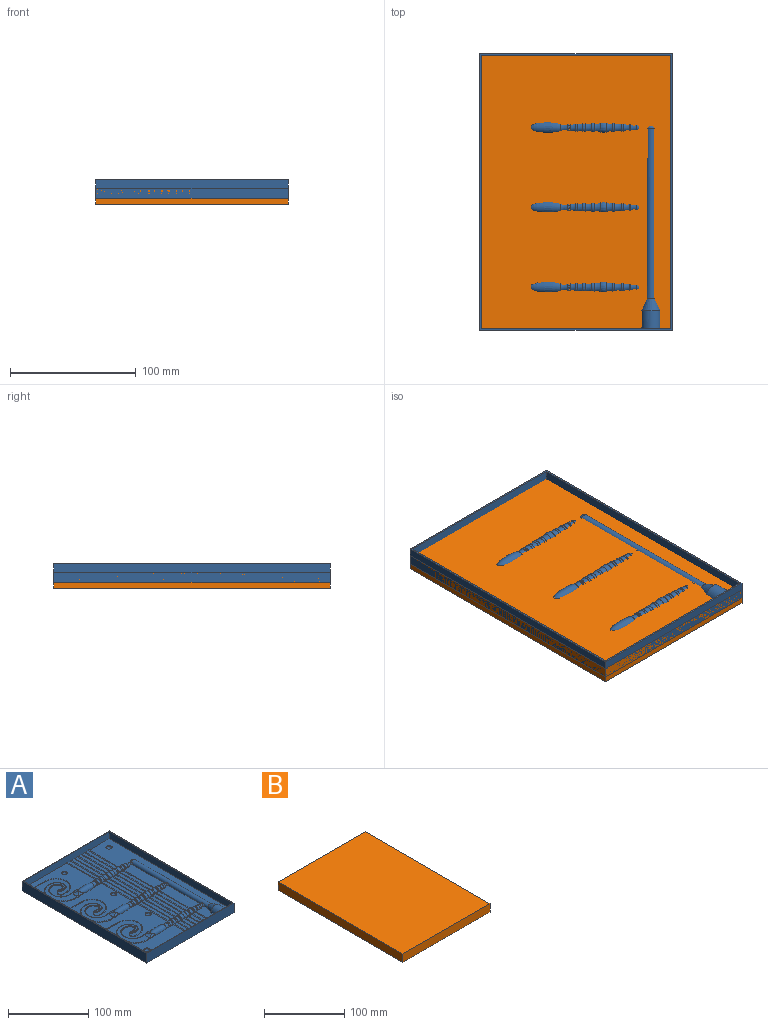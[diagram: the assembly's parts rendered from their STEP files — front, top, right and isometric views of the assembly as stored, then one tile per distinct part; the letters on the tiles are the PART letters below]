
ASSEMBLY  parts=2 mates=1
PART A: 197 faces, bbox 154.9x221.7x16.3 mm
  f0: plane 30.21x16.13mm, normal (0,0,1), area 393mm2, adj f10,f56,f113,f114,f116,f121,f146,f147
  f1: plane 28.08x5.08mm, normal (0,0,1), area 141.8mm2, adj f10,f17,f117,f185,f189,f196
  f2: plane 59.75x16.13mm, normal (0,0,1), area 919.8mm2, adj f9,f10,f56,f85,f86,f88,f93,f113
  f3: plane 55.56x5.08mm, normal (0,0,1), area 280.6mm2, adj f9,f10,f16,f17,f89,f117,f186,f190
  f4: plane 59.75x16.13mm, normal (0,0,1), area 919.8mm2, adj f8,f9,f56,f57,f58,f60,f65,f85
  f5: plane 55.56x5.08mm, normal (0,0,1), area 280.6mm2, adj f8,f9,f15,f16,f61,f89,f187,f191
  f6: plane 215.62x35.02mm, normal (0,0,1), area 3518.5mm2, adj f8,f56,f57,f58,f60,f65,f141,f142
  f7: plane 52.59x5.08mm, normal (0,0,1), area 266.3mm2, adj f8,f15,f61,f188,f192,f193
  f8: torus R=13.95mm, axis (-1,0,0), area 51.1mm2, adj f4,f5,f6,f7,f60,f61,f191,f192
  f9: torus R=13.95mm, axis (-1,0,0), area 51.1mm2, adj f2,f3,f4,f5,f88,f89,f190,f191
  f10: torus R=13.95mm, axis (-1,0,0), area 51.1mm2, adj f0,f1,f2,f3,f116,f117,f189,f190
  f11: plane 27.89x5.08mm, normal (0,0,1), area 140.4mm2, adj f17,f24,f118,f181,f185,f196
  f12: plane 55.18x5.08mm, normal (0,0,1), area 277.7mm2, adj f16,f17,f23,f24,f90,f118,f182,f186
  f13: plane 55.18x5.08mm, normal (0,0,1), area 277.7mm2, adj f15,f16,f22,f23,f62,f90,f183,f187
  f14: plane 52.4x5.08mm, normal (0,0,1), area 264.9mm2, adj f15,f22,f62,f184,f188,f193
  f15: torus R=14.13mm, axis (1,0,0), area 64.7mm2, adj f5,f7,f13,f14,f61,f62,f187,f188
  f16: torus R=14.13mm, axis (1,0,0), area 64.7mm2, adj f3,f5,f12,f13,f89,f90,f186,f187
  f17: torus R=14.13mm, axis (1,0,0), area 64.7mm2, adj f1,f3,f11,f12,f117,f118,f185,f186
  f18: plane 27.6x5.08mm, normal (0,0,1), area 138mm2, adj f24,f33,f177,f181,f196
  f19: plane 54.6x5.08mm, normal (0,0,1), area 272.9mm2, adj f23,f24,f31,f33,f178,f182
  f20: plane 54.6x5.08mm, normal (0,0,1), area 272.9mm2, adj f22,f23,f29,f31,f179,f183
  f21: plane 52.11x5.08mm, normal (0,0,1), area 262.5mm2, adj f22,f29,f180,f184,f193
  f22: torus R=14.5mm, axis (-1,0,0), area 64.6mm2, adj f13,f14,f20,f21,f29,f62,f183,f184
  f23: torus R=14.5mm, axis (-1,0,0), area 64.6mm2, adj f12,f13,f19,f20,f31,f90,f182,f183
  f24: torus R=14.5mm, axis (-1,0,0), area 64.6mm2, adj f11,f12,f18,f19,f33,f118,f181,f182
  f25: plane 27.76x5.08mm, normal (0,0,1), area 140.5mm2, adj f34,f41,f173,f177,f196
  f26: plane 54.91x5.08mm, normal (0,0,1), area 277.9mm2, adj f32,f34,f40,f41,f174,f178
  f27: plane 54.91x5.08mm, normal (0,0,1), area 277.9mm2, adj f30,f32,f39,f40,f175,f179
  f28: plane 52.27x5.08mm, normal (0,0,1), area 265mm2, adj f30,f39,f176,f180,f193
  f29: revolved ~10.16x5.08mm, area 74.3mm2, adj f20,f21,f22,f30,f179,f180
  f30: torus R=14.45mm, axis (-1,0,0), area 68.5mm2, adj f27,f28,f29,f39,f179,f180
  f31: revolved ~10.16x5.08mm, area 74.3mm2, adj f19,f20,f23,f32,f178,f179
  f32: torus R=14.45mm, axis (-1,0,0), area 68.5mm2, adj f26,f27,f31,f40,f178,f179
  f33: revolved ~10.16x5.08mm, area 74.3mm2, adj f18,f19,f24,f34,f177,f178
  f34: torus R=14.45mm, axis (-1,0,0), area 68.5mm2, adj f25,f26,f33,f41,f177,f178
  f35: plane 27.95x5.08mm, normal (0,0,1), area 141.4mm2, adj f41,f48,f122,f169,f173,f196
  f36: plane 55.28x5.08mm, normal (0,0,1), area 279.7mm2, adj f40,f41,f47,f48,f94,f122,f170,f174
  f37: plane 55.28x5.08mm, normal (0,0,1), area 279.7mm2, adj f39,f40,f46,f47,f66,f94,f171,f175
  f38: plane 52.45x5.08mm, normal (0,0,1), area 265.9mm2, adj f39,f46,f66,f172,f176,f193
  f39: sphere r=4.57mm, area 27.8mm2, adj f27,f28,f30,f37,f38,f66,f175,f176
  f40: sphere r=4.57mm, area 27.8mm2, adj f26,f27,f32,f36,f37,f94,f174,f175
  f41: sphere r=4.57mm, area 27.8mm2, adj f25,f26,f34,f35,f36,f122,f173,f174
  f42: plane 28x5.08mm, normal (0,0,1), area 141.7mm2, adj f48,f54,f123,f165,f169,f196
  f43: plane 55.4x5.08mm, normal (0,0,1), area 280.2mm2, adj f47,f48,f53,f54,f95,f123,f167,f170
  f44: plane 55.4x5.08mm, normal (0,0,1), area 280.2mm2, adj f46,f47,f52,f53,f67,f95,f168,f171
  f45: plane 52.51x5.08mm, normal (0,0,1), area 266.2mm2, adj f46,f52,f67,f166,f172,f193
  f46: revolved ~8.88x4.44mm, area 30.1mm2, adj f37,f38,f44,f45,f66,f67,f171,f172
  f47: revolved ~8.88x4.44mm, area 30.1mm2, adj f36,f37,f43,f44,f94,f95,f170,f171
  f48: revolved ~8.88x4.44mm, area 30.1mm2, adj f35,f36,f42,f43,f122,f123,f169,f170
  f49: plane 79.31x74.46mm, normal (0,0,1), area 3032.8mm2, adj f54,f115,f119,f120,f124,f125,f133,f134
  f50: plane 107.13x74.46mm, normal (0,0,1), area 3584.8mm2, adj f53,f54,f87,f91,f92,f96,f97,f105
  f51: plane 107.13x74.46mm, normal (0,0,1), area 3584.8mm2, adj f52,f53,f59,f63,f64,f68,f69,f77
  f52: revolved ~8.64x4.32mm, area 25.6mm2, adj f44,f45,f51,f55,f67,f68,f166,f168
  f53: revolved ~8.64x4.32mm, area 25.6mm2, adj f43,f44,f50,f51,f95,f96,f167,f168
  f54: revolved ~8.64x4.32mm, area 25.6mm2, adj f42,f43,f49,f50,f123,f124,f165,f167
  f55: plane 74.46x52.94mm, normal (0,0,1), area 2375mm2, adj f52,f63,f64,f68,f69,f70,f76,f78
  f56: cylinder r=4.06mm len=135.26mm, axis (0,1,0), area 1691.3mm2, adj f0,f2,f4,f6,f142,f143,f145,f146
  f57: cylinder r=1.91mm len=6.76mm, axis (-1,0,0), area 25.6mm2, adj f4,f6,f58,f143,f144
  f58: sphere r=3.56mm, area 38.8mm2, adj f4,f6,f57,f65
  f59: extruded ~44.23x34.95mm, area 31.1mm2, adj f51,f72,f77,f84
  f60: revolved ~7.87x3.94mm, area 16.9mm2, adj f4,f6,f8,f65
  f61: sphere r=4.32mm, area 28.5mm2, adj f5,f7,f8,f15
  f62: sphere r=4.57mm, area 30.3mm2, adj f13,f14,f15,f22
  f63: revolved ~8.13x4.06mm, area 30.6mm2, adj f51,f55,f68,f69
  f64: revolved ~24.32x10.22mm, area 309.6mm2, adj f51,f55,f69,f73,f74,f75,f76,f77
  f65: torus R=13.59mm, axis (-1,0,0), area 46.1mm2, adj f4,f6,f58,f60
  f66: torus R=14.27mm, axis (-1,0,0), area 61.7mm2, adj f37,f38,f39,f46
  f67: torus R=14.21mm, axis (-1,0,0), area 54.9mm2, adj f44,f45,f46,f52
  f68: torus R=14.03mm, axis (-1,0,0), area 50.6mm2, adj f51,f52,f55,f63
  f69: torus R=13.79mm, axis (-1,0,0), area 61.6mm2, adj f51,f55,f63,f64
  f70: extruded ~30.25x28.18mm, area 22.2mm2, adj f55,f72,f76,f83
  f71: plane 43.04x31.63mm, normal (0,0,1), area 466.1mm2, adj f72,f73
  f72: bspline ~44.26x36.96mm, area 205.5mm2, adj f59,f70,f71,f74,f75,f82
  f73: bspline ~13.54x7.76mm, area 42.8mm2, adj f64,f71,f74,f75
  f74: bspline ~15.12x5.32mm, area 44.6mm2, adj f64,f72,f73,f76
  f75: bspline ~10.58x3.79mm, area 20.6mm2, adj f64,f72,f73,f77
  f76: bspline ~4.98x1.36mm, area 0.8mm2, adj f55,f64,f70,f74
  f77: bspline ~2.25x1.56mm, area 0.4mm2, adj f51,f59,f64,f75
  f78: cylinder r=0.38mm len=28.6mm, axis (1,0,0), area 34.2mm2, adj f51,f55,f79,f194
  f79: torus R=17.78mm, axis (0,0,-1), area 66.9mm2, adj f51,f55,f78,f80
  f80: cylinder r=0.38mm len=4.56mm, axis (-1,0,0), area 5.5mm2, adj f51,f55,f79,f81
  f81: torus R=4.45mm, axis (0,0,-1), area 15.6mm2, adj f51,f55,f80,f82,f83,f84
  f82: bspline ~1.34x0.76mm, area 0.6mm2, adj f72,f81,f83,f84
  f83: bspline ~0.39x0.37mm, area 0.1mm2, adj f55,f70,f81,f82
  f84: bspline ~0.62x0.51mm, area 0.1mm2, adj f51,f59,f81,f82
  f85: cylinder r=1.91mm len=3.81mm, axis (-1,0,0), area 18.4mm2, adj f2,f4,f86,f145
  f86: sphere r=3.56mm, area 38.8mm2, adj f2,f4,f85,f93
  f87: extruded ~44.23x34.95mm, area 31.1mm2, adj f50,f100,f105,f112
  f88: revolved ~7.87x3.94mm, area 16.9mm2, adj f2,f4,f9,f93
  f89: sphere r=4.32mm, area 28.5mm2, adj f3,f5,f9,f16
  f90: sphere r=4.57mm, area 30.3mm2, adj f12,f13,f16,f23
  f91: revolved ~8.13x4.06mm, area 30.6mm2, adj f50,f51,f96,f97
  f92: revolved ~24.32x10.22mm, area 309.6mm2, adj f50,f51,f97,f101,f102,f103,f104,f105
  f93: torus R=13.59mm, axis (-1,0,0), area 46.1mm2, adj f2,f4,f86,f88
  f94: torus R=14.27mm, axis (-1,0,0), area 61.7mm2, adj f36,f37,f40,f47
  f95: torus R=14.21mm, axis (-1,0,0), area 54.9mm2, adj f43,f44,f47,f53
  f96: torus R=14.03mm, axis (-1,0,0), area 50.6mm2, adj f50,f51,f53,f91
  f97: torus R=13.79mm, axis (-1,0,0), area 61.6mm2, adj f50,f51,f91,f92
  f98: extruded ~30.25x28.18mm, area 22.2mm2, adj f51,f100,f104,f111
  f99: plane 43.04x31.63mm, normal (0,0,1), area 466.1mm2, adj f100,f101
  f100: bspline ~44.26x36.96mm, area 205.5mm2, adj f87,f98,f99,f102,f103,f110
  f101: bspline ~13.54x7.76mm, area 42.8mm2, adj f92,f99,f102,f103
  f102: bspline ~15.12x5.32mm, area 44.6mm2, adj f92,f100,f101,f104
  f103: bspline ~10.58x3.79mm, area 20.6mm2, adj f92,f100,f101,f105
  f104: bspline ~4.98x1.79mm, area 0.8mm2, adj f51,f92,f98,f102
  f105: bspline ~2.25x1.56mm, area 0.4mm2, adj f50,f87,f92,f103
  f106: cylinder r=0.38mm len=28.6mm, axis (1,0,0), area 34.2mm2, adj f50,f51,f107,f194
  f107: torus R=17.78mm, axis (0,0,-1), area 66.9mm2, adj f50,f51,f106,f108
  f108: cylinder r=0.38mm len=4.56mm, axis (-1,0,0), area 5.5mm2, adj f50,f51,f107,f109
  f109: torus R=4.45mm, axis (0,0,-1), area 15.6mm2, adj f50,f51,f108,f110,f111,f112
  f110: bspline ~1.34x0.76mm, area 0.6mm2, adj f100,f109,f111,f112
  f111: bspline ~0.39x0.37mm, area 0.1mm2, adj f51,f98,f109,f110
  f112: bspline ~0.62x0.51mm, area 0.1mm2, adj f50,f87,f109,f110
  f113: cylinder r=1.91mm len=3.81mm, axis (-1,0,0), area 18.4mm2, adj f0,f2,f114,f146
  f114: sphere r=3.56mm, area 38.8mm2, adj f0,f2,f113,f121
  f115: extruded ~44.23x34.95mm, area 31.1mm2, adj f49,f128,f133,f140
  f116: revolved ~7.87x3.94mm, area 16.9mm2, adj f0,f2,f10,f121
  f117: sphere r=4.32mm, area 28.5mm2, adj f1,f3,f10,f17
  f118: sphere r=4.57mm, area 30.3mm2, adj f11,f12,f17,f24
  f119: revolved ~8.13x4.06mm, area 30.6mm2, adj f49,f50,f124,f125
  f120: revolved ~24.32x10.22mm, area 309.6mm2, adj f49,f50,f125,f129,f130,f131,f132,f133
  f121: torus R=13.59mm, axis (-1,0,0), area 46.1mm2, adj f0,f2,f114,f116
  f122: torus R=14.27mm, axis (-1,0,0), area 61.7mm2, adj f35,f36,f41,f48
  f123: torus R=14.21mm, axis (-1,0,0), area 54.9mm2, adj f42,f43,f48,f54
  f124: torus R=14.03mm, axis (-1,0,0), area 50.6mm2, adj f49,f50,f54,f119
  f125: torus R=13.79mm, axis (-1,0,0), area 61.6mm2, adj f49,f50,f119,f120
  f126: extruded ~30.25x28.18mm, area 22.2mm2, adj f50,f128,f132,f139
  f127: plane 43.04x31.63mm, normal (0,0,1), area 466.1mm2, adj f128,f129
  f128: bspline ~44.26x36.96mm, area 205.5mm2, adj f115,f126,f127,f130,f131,f138
  f129: bspline ~13.54x7.76mm, area 42.8mm2, adj f120,f127,f130,f131
  f130: bspline ~15.12x5.32mm, area 44.6mm2, adj f120,f128,f129,f132
  f131: bspline ~10.58x3.79mm, area 20.6mm2, adj f120,f128,f129,f133
  f132: bspline ~4.98x1.36mm, area 0.8mm2, adj f50,f120,f126,f130
  f133: bspline ~2.25x1.56mm, area 0.4mm2, adj f49,f115,f120,f131
  f134: cylinder r=0.38mm len=28.6mm, axis (1,0,0), area 34.2mm2, adj f49,f50,f135,f194
  f135: torus R=17.78mm, axis (0,0,-1), area 66.9mm2, adj f49,f50,f134,f136
  f136: cylinder r=0.38mm len=4.56mm, axis (-1,0,0), area 5.5mm2, adj f49,f50,f135,f137
  f137: torus R=4.45mm, axis (0,0,-1), area 15.6mm2, adj f49,f50,f136,f138,f139,f140
  f138: bspline ~1.34x0.76mm, area 0.6mm2, adj f128,f137,f139,f140
  f139: bspline ~0.39x0.37mm, area 0.1mm2, adj f50,f126,f137,f138
  f140: bspline ~0.62x0.51mm, area 0.1mm2, adj f49,f115,f137,f138
  f141: plane 3.05x1.52mm, normal (0,1,0), area 3.6mm2, adj f6,f142
  f142: torus R=1.52mm, axis (0,-1,0), area 31.8mm2, adj f6,f56,f141,f144
  f143: bspline ~3.73x2.86mm, area 7.4mm2, adj f4,f56,f57,f144
  f144: bspline ~3.06x2.57mm, area 2.6mm2, adj f57,f142,f143
  f145: bspline ~7.37x2.69mm, area 16.4mm2, adj f2,f4,f56,f85
  f146: bspline ~7.37x2.69mm, area 16.4mm2, adj f0,f2,f56,f113
  f147: cylinder r=8mm len=16mm, axis (0,-1,0), area 334.9mm2, adj f0,f6,f148,f196
  f148: cone r=8.13mm half-angle=21.8deg, axis (0,-1,0), area 200.9mm2, adj f0,f6,f56,f147
  f149: plane 153.31x14.73mm, normal (0,-1,0), area 2258.6mm2, adj f150,f152,f153,f154
  f150: plane 220.09x153.31mm, normal (0,0,1), area 942mm2, adj f149,f151,f152,f153,f193,f194,f195,f196
  f151: plane 153.31x14.73mm, normal (0,1,0), area 2258.6mm2, adj f150,f152,f153,f154
  f152: plane 220.09x14.73mm, normal (1,0,0), area 3242.3mm2, adj f149,f150,f151,f154
  f153: plane 220.09x14.73mm, normal (-1,0,0), area 3242.3mm2, adj f149,f150,f151,f154
  f154: plane 220.09x153.31mm, normal (0,0,-1), area 33742.1mm2, adj f149,f151,f152,f153
  f155: sphere r=3.17mm, area 52.5mm2, adj f162
  f156: sphere r=3.17mm, area 52.5mm2, adj f160
  f157: sphere r=3.17mm, area 52.5mm2, adj f161
  f158: sphere r=3.17mm, area 51.1mm2, adj f163
  f159: sphere r=3.17mm, area 51.1mm2, adj f164
  f160: cone r=3.11mm half-angle=50.6deg, axis (0,0,1), area 21.2mm2, adj f6,f156
  f161: cone r=3.11mm half-angle=50.6deg, axis (0,0,1), area 21.2mm2, adj f55,f157
  f162: cone r=3.11mm half-angle=50.6deg, axis (0,0,1), area 21.2mm2, adj f49,f155
  f163: cone r=3.11mm half-angle=50.6deg, axis (0,0,1), area 21.2mm2, adj f51,f158
  f164: cone r=3.11mm half-angle=50.6deg, axis (0,0,1), area 21.2mm2, adj f50,f159
  f165: cylinder r=0.64mm len=27.82mm, axis (0,1,0), area 55.4mm2, adj f42,f49,f54,f196
  f166: cylinder r=0.64mm len=52.32mm, axis (0,1,0), area 104.3mm2, adj f45,f52,f55,f193
  f167: cylinder r=0.64mm len=55.03mm, axis (0,1,0), area 109.6mm2, adj f43,f50,f53,f54
  f168: cylinder r=0.64mm len=55.03mm, axis (0,1,0), area 109.6mm2, adj f44,f51,f52,f53
  f169: cylinder r=0.64mm len=27.7mm, axis (0,1,0), area 55.2mm2, adj f35,f42,f48,f196
  f170: cylinder r=0.64mm len=54.8mm, axis (0,1,0), area 109.2mm2, adj f36,f43,f47,f48
  f171: cylinder r=0.64mm len=54.8mm, axis (0,1,0), area 109.2mm2, adj f37,f44,f46,f47
  f172: cylinder r=0.64mm len=52.21mm, axis (0,1,0), area 104.1mm2, adj f38,f45,f46,f193
  f173: cylinder r=0.64mm len=27.55mm, axis (0,1,0), area 54.9mm2, adj f25,f35,f41,f196
  f174: cylinder r=0.64mm len=54.5mm, axis (0,1,0), area 108.6mm2, adj f26,f36,f40,f41
  f175: cylinder r=0.64mm len=54.5mm, axis (0,1,0), area 108.6mm2, adj f27,f37,f39,f40
  f176: cylinder r=0.64mm len=52.06mm, axis (0,1,0), area 103.8mm2, adj f28,f38,f39,f193
  f177: cylinder r=0.64mm len=27.4mm, axis (0,1,0), area 54.4mm2, adj f18,f25,f33,f34,f196
  f178: cylinder r=0.64mm len=54.18mm, axis (0,1,0), area 107.6mm2, adj f19,f26,f31,f32,f33,f34
  f179: cylinder r=0.64mm len=54.18mm, axis (0,1,0), area 107.6mm2, adj f20,f27,f29,f30,f31,f32
  f180: cylinder r=0.64mm len=51.9mm, axis (0,1,0), area 103.3mm2, adj f21,f28,f29,f30,f193
  f181: cylinder r=0.64mm len=27.72mm, axis (0,1,0), area 55.2mm2, adj f11,f18,f24,f196
  f182: cylinder r=0.64mm len=54.82mm, axis (0,1,0), area 109.1mm2, adj f12,f19,f23,f24
  f183: cylinder r=0.64mm len=54.82mm, axis (0,1,0), area 109.1mm2, adj f13,f20,f22,f23
  f184: cylinder r=0.64mm len=52.22mm, axis (0,1,0), area 104.1mm2, adj f14,f21,f22,f193
  f185: cylinder r=0.64mm len=28.06mm, axis (0,1,0), area 55.8mm2, adj f1,f11,f17,f196
  f186: cylinder r=0.64mm len=55.51mm, axis (0,1,0), area 110.4mm2, adj f3,f12,f16,f17
  f187: cylinder r=0.64mm len=55.51mm, axis (0,1,0), area 110.4mm2, adj f5,f13,f15,f16
  f188: cylinder r=0.64mm len=52.57mm, axis (0,1,0), area 104.7mm2, adj f7,f14,f15,f193
  f189: cylinder r=0.64mm len=28.18mm, axis (0,1,0), area 56mm2, adj f0,f1,f10,f196
  f190: cylinder r=0.64mm len=55.74mm, axis (0,1,0), area 110.7mm2, adj f2,f3,f9,f10
  f191: cylinder r=0.64mm len=55.74mm, axis (0,1,0), area 110.7mm2, adj f4,f5,f8,f9
  f192: cylinder r=0.64mm len=52.68mm, axis (0,1,0), area 104.8mm2, adj f6,f7,f8,f193
  f193: plane 150.9x9.78mm, normal (0,-1,0.1), area 1448.7mm2, adj f6,f7,f14,f21,f28,f38,f45,f55
  f194: plane 217.62x9.73mm, normal (1,0,0.1), area 2100.2mm2, adj f49,f50,f51,f55,f78,f106,f134,f150
  f195: plane 217.55x9.65mm, normal (-1,0,0.1), area 2100.9mm2, adj f6,f150,f193,f196
  f196: plane 152.37x11.25mm, normal (0,1,0.1), area 1347.6mm2, adj f0,f1,f6,f11,f18,f25,f35,f42
PART B: 192 faces, bbox 154.9x221.7x14.3 mm
  f0: plane 152.37x11.25mm, normal (0,1,-0.1), area 1347.6mm2, adj f1,f5,f9,f13,f17,f21,f25,f29
  f1: plane 28.08x5.08mm, normal (0,0,-1), area 141.8mm2, adj f0,f97,f106,f107,f186,f190
  f2: plane 55.56x5.08mm, normal (0,0,-1), area 280.6mm2, adj f67,f76,f77,f97,f106,f107,f187,f191
  f3: plane 52.59x5.08mm, normal (0,0,-1), area 266.3mm2, adj f37,f46,f47,f162,f184,f188
  f4: plane 55.56x5.08mm, normal (0,0,-1), area 280.6mm2, adj f37,f46,f47,f67,f76,f77,f185,f189
  f5: plane 27.89x5.08mm, normal (0,0,-1), area 140.4mm2, adj f0,f98,f107,f108,f182,f186
  f6: plane 55.18x5.08mm, normal (0,0,-1), area 277.7mm2, adj f68,f77,f78,f98,f107,f108,f183,f187
  f7: plane 52.4x5.08mm, normal (0,0,-1), area 264.9mm2, adj f38,f47,f48,f162,f180,f184
  f8: plane 55.18x5.08mm, normal (0,0,-1), area 277.7mm2, adj f38,f47,f48,f68,f77,f78,f181,f185
  f9: plane 27.6x5.08mm, normal (0,0,-1), area 138mm2, adj f0,f99,f108,f178,f182
  f10: plane 54.6x5.08mm, normal (0,0,-1), area 272.9mm2, adj f69,f78,f99,f108,f179,f183
  f11: plane 52.11x5.08mm, normal (0,0,-1), area 262.5mm2, adj f39,f48,f162,f176,f180
  f12: plane 54.6x5.08mm, normal (0,0,-1), area 272.9mm2, adj f39,f48,f69,f78,f177,f181
  f13: plane 27.76x5.08mm, normal (0,0,-1), area 140.5mm2, adj f0,f100,f109,f174,f178
  f14: plane 54.91x5.08mm, normal (0,0,-1), area 277.9mm2, adj f70,f79,f100,f109,f175,f179
  f15: plane 52.27x5.08mm, normal (0,0,-1), area 265mm2, adj f40,f49,f162,f172,f176
  f16: plane 54.91x5.08mm, normal (0,0,-1), area 277.9mm2, adj f40,f49,f70,f79,f173,f177
  f17: plane 27.95x5.08mm, normal (0,0,-1), area 141.4mm2, adj f0,f100,f101,f110,f170,f174
  f18: plane 55.28x5.08mm, normal (0,0,-1), area 279.7mm2, adj f70,f71,f80,f100,f101,f110,f171,f175
  f19: plane 52.45x5.08mm, normal (0,0,-1), area 265.9mm2, adj f40,f41,f50,f162,f168,f172
  f20: plane 55.28x5.08mm, normal (0,0,-1), area 279.7mm2, adj f40,f41,f50,f70,f71,f80,f169,f173
  f21: plane 28x5.08mm, normal (0,0,-1), area 141.7mm2, adj f0,f101,f102,f111,f166,f170
  f22: plane 55.4x5.08mm, normal (0,0,-1), area 280.2mm2, adj f71,f72,f81,f101,f102,f111,f167,f171
  f23: plane 52.51x5.08mm, normal (0,0,-1), area 266.2mm2, adj f41,f42,f51,f162,f164,f168
  f24: plane 55.4x5.08mm, normal (0,0,-1), area 280.2mm2, adj f41,f42,f51,f71,f72,f81,f165,f169
  f25: plane 79.31x74.46mm, normal (0,0,-1), area 3048mm2, adj f0,f95,f102,f103,f104,f112,f113,f116
  f26: plane 107.13x74.46mm, normal (0,0,-1), area 3600mm2, adj f65,f72,f73,f74,f82,f83,f86,f87
  f27: plane 74.46x52.94mm, normal (0,0,-1), area 2390.2mm2, adj f42,f43,f44,f52,f53,f54,f55,f57
  f28: plane 107.13x74.46mm, normal (0,0,-1), area 3600mm2, adj f35,f42,f43,f44,f52,f53,f56,f57
  f29: plane 30.21x16.13mm, normal (0,0,-1), area 393mm2, adj f0,f32,f93,f94,f96,f105,f106,f127
  f30: plane 59.75x16.13mm, normal (0,0,-1), area 919.8mm2, adj f32,f63,f64,f66,f75,f76,f93,f94
  f31: plane 215.62x35.02mm, normal (0,0,-1), area 3533.7mm2, adj f0,f32,f33,f34,f36,f45,f46,f123
  f32: cylinder r=4.06mm len=135.26mm, axis (0,1,0), area 1691.3mm2, adj f29,f30,f31,f124,f125,f126,f127,f129
  f33: cylinder r=1.91mm len=6.76mm, axis (-1,0,0), area 25.6mm2, adj f31,f34,f125,f148,f149
  f34: sphere r=3.56mm, area 38.8mm2, adj f31,f33,f45,f149
  f35: extruded ~44.23x34.95mm, area 31.1mm2, adj f28,f56,f62,f131
  f36: revolved ~7.87x3.94mm, area 16.9mm2, adj f31,f45,f46,f149
  f37: sphere r=4.32mm, area 28.5mm2, adj f3,f4,f46,f47
  f38: sphere r=4.57mm, area 30.3mm2, adj f7,f8,f47,f48
  f39: revolved ~10.16x5.08mm, area 74.3mm2, adj f11,f12,f48,f49,f176,f177
  f40: sphere r=4.57mm, area 27.8mm2, adj f15,f16,f19,f20,f49,f50,f172,f173
  f41: revolved ~8.88x4.44mm, area 30.1mm2, adj f19,f20,f23,f24,f50,f51,f168,f169
  f42: revolved ~8.64x4.32mm, area 25.6mm2, adj f23,f24,f27,f28,f51,f52,f164,f165
  f43: revolved ~8.13x4.06mm, area 30.6mm2, adj f27,f28,f52,f53
  f44: revolved ~24.32x10.22mm, area 309.6mm2, adj f27,f28,f53,f55,f56,f132,f133,f134
  f45: torus R=13.59mm, axis (-1,0,0), area 46.1mm2, adj f31,f34,f36,f149
  f46: torus R=13.95mm, axis (-1,0,0), area 51.1mm2, adj f3,f4,f31,f36,f37,f149,f188,f189
  f47: torus R=14.13mm, axis (1,0,0), area 64.7mm2, adj f3,f4,f7,f8,f37,f38,f184,f185
  f48: torus R=14.5mm, axis (-1,0,0), area 64.6mm2, adj f7,f8,f11,f12,f38,f39,f180,f181
  f49: torus R=14.45mm, axis (-1,0,0), area 68.5mm2, adj f15,f16,f39,f40,f176,f177
  f50: torus R=14.27mm, axis (-1,0,0), area 61.7mm2, adj f19,f20,f40,f41
  f51: torus R=14.21mm, axis (-1,0,0), area 54.9mm2, adj f23,f24,f41,f42
  f52: torus R=14.03mm, axis (-1,0,0), area 50.6mm2, adj f27,f28,f42,f43
  f53: torus R=13.79mm, axis (-1,0,0), area 61.6mm2, adj f27,f28,f43,f44
  f54: extruded ~30.25x28.18mm, area 22.2mm2, adj f27,f55,f61,f131
  f55: bspline ~4.98x1.79mm, area 0.8mm2, adj f27,f44,f54,f132
  f56: bspline ~2.25x1.56mm, area 0.4mm2, adj f28,f35,f44,f133
  f57: cylinder r=0.38mm len=28.6mm, axis (1,0,0), area 34.2mm2, adj f27,f28,f58,f163
  f58: torus R=17.78mm, axis (0,0,-1), area 66.9mm2, adj f27,f28,f57,f59
  f59: cylinder r=0.38mm len=4.56mm, axis (-1,0,0), area 5.5mm2, adj f27,f28,f58,f60
  f60: torus R=4.45mm, axis (0,0,-1), area 15.6mm2, adj f27,f28,f59,f61,f62,f135
  f61: bspline ~0.57x0.43mm, area 0.1mm2, adj f27,f54,f60,f135
  f62: bspline ~0.6x0.46mm, area 0.1mm2, adj f28,f35,f60,f135
  f63: cylinder r=1.91mm len=3.81mm, axis (-1,0,0), area 18.4mm2, adj f30,f64,f126,f149
  f64: sphere r=3.56mm, area 38.8mm2, adj f30,f63,f75,f149
  f65: extruded ~44.23x34.95mm, area 31.1mm2, adj f26,f86,f92,f137
  f66: revolved ~7.87x3.94mm, area 16.9mm2, adj f30,f75,f76,f149
  f67: sphere r=4.32mm, area 28.5mm2, adj f2,f4,f76,f77
  f68: sphere r=4.57mm, area 30.3mm2, adj f6,f8,f77,f78
  f69: revolved ~10.16x5.08mm, area 74.3mm2, adj f10,f12,f78,f79,f177,f179
  f70: sphere r=4.57mm, area 27.8mm2, adj f14,f16,f18,f20,f79,f80,f173,f175
  f71: revolved ~8.88x4.44mm, area 30.1mm2, adj f18,f20,f22,f24,f80,f81,f169,f171
  f72: revolved ~8.64x4.32mm, area 25.6mm2, adj f22,f24,f26,f28,f81,f82,f165,f167
  f73: revolved ~8.13x4.06mm, area 30.6mm2, adj f26,f28,f82,f83
  f74: revolved ~24.32x10.22mm, area 309.6mm2, adj f26,f28,f83,f85,f86,f138,f139,f140
  f75: torus R=13.59mm, axis (-1,0,0), area 46.1mm2, adj f30,f64,f66,f149
  f76: torus R=13.95mm, axis (-1,0,0), area 51.1mm2, adj f2,f4,f30,f66,f67,f149,f189,f191
  f77: torus R=14.13mm, axis (1,0,0), area 64.7mm2, adj f2,f4,f6,f8,f67,f68,f185,f187
  f78: torus R=14.5mm, axis (-1,0,0), area 64.6mm2, adj f6,f8,f10,f12,f68,f69,f181,f183
  f79: torus R=14.45mm, axis (-1,0,0), area 68.5mm2, adj f14,f16,f69,f70,f177,f179
  f80: torus R=14.27mm, axis (-1,0,0), area 61.7mm2, adj f18,f20,f70,f71
  f81: torus R=14.21mm, axis (-1,0,0), area 54.9mm2, adj f22,f24,f71,f72
  f82: torus R=14.03mm, axis (-1,0,0), area 50.6mm2, adj f26,f28,f72,f73
  f83: torus R=13.79mm, axis (-1,0,0), area 61.6mm2, adj f26,f28,f73,f74
  f84: extruded ~30.25x28.18mm, area 22.2mm2, adj f28,f85,f91,f137
  f85: bspline ~4.98x1.79mm, area 0.8mm2, adj f28,f74,f84,f138
  f86: bspline ~2.25x1.56mm, area 0.4mm2, adj f26,f65,f74,f139
  f87: cylinder r=0.38mm len=28.6mm, axis (1,0,0), area 34.2mm2, adj f26,f28,f88,f163
  f88: torus R=17.78mm, axis (0,0,-1), area 66.9mm2, adj f26,f28,f87,f89
  f89: cylinder r=0.38mm len=4.56mm, axis (-1,0,0), area 5.5mm2, adj f26,f28,f88,f90
  f90: torus R=4.45mm, axis (0,0,-1), area 15.6mm2, adj f26,f28,f89,f91,f92,f141
  f91: bspline ~0.57x0.43mm, area 0.1mm2, adj f28,f84,f90,f141
  f92: bspline ~0.6x0.46mm, area 0.1mm2, adj f26,f65,f90,f141
  f93: cylinder r=1.91mm len=3.81mm, axis (-1,0,0), area 18.4mm2, adj f29,f30,f94,f127
  f94: sphere r=3.56mm, area 38.8mm2, adj f29,f30,f93,f105
  f95: extruded ~44.23x34.95mm, area 31.1mm2, adj f25,f116,f122,f143
  f96: revolved ~7.87x3.94mm, area 16.9mm2, adj f29,f30,f105,f106
  f97: sphere r=4.32mm, area 28.5mm2, adj f1,f2,f106,f107
  f98: sphere r=4.57mm, area 30.3mm2, adj f5,f6,f107,f108
  f99: revolved ~10.16x5.08mm, area 74.3mm2, adj f9,f10,f108,f109,f178,f179
  f100: sphere r=4.57mm, area 27.8mm2, adj f13,f14,f17,f18,f109,f110,f174,f175
  f101: revolved ~8.88x4.44mm, area 30.1mm2, adj f17,f18,f21,f22,f110,f111,f170,f171
  f102: revolved ~8.64x4.32mm, area 25.6mm2, adj f21,f22,f25,f26,f111,f112,f166,f167
  f103: revolved ~8.13x4.06mm, area 30.6mm2, adj f25,f26,f112,f113
  f104: revolved ~24.32x10.22mm, area 309.6mm2, adj f25,f26,f113,f115,f116,f144,f145,f146
  f105: torus R=13.59mm, axis (-1,0,0), area 46.1mm2, adj f29,f30,f94,f96
  f106: torus R=13.95mm, axis (-1,0,0), area 51.1mm2, adj f1,f2,f29,f30,f96,f97,f190,f191
  f107: torus R=14.13mm, axis (1,0,0), area 64.7mm2, adj f1,f2,f5,f6,f97,f98,f186,f187
  f108: torus R=14.5mm, axis (-1,0,0), area 64.6mm2, adj f5,f6,f9,f10,f98,f99,f182,f183
  f109: torus R=14.45mm, axis (-1,0,0), area 68.5mm2, adj f13,f14,f99,f100,f178,f179
  f110: torus R=14.27mm, axis (-1,0,0), area 61.7mm2, adj f17,f18,f100,f101
  f111: torus R=14.21mm, axis (-1,0,0), area 54.9mm2, adj f21,f22,f101,f102
  f112: torus R=14.03mm, axis (-1,0,0), area 50.6mm2, adj f25,f26,f102,f103
  f113: torus R=13.79mm, axis (-1,0,0), area 61.6mm2, adj f25,f26,f103,f104
  f114: extruded ~30.25x28.18mm, area 22.2mm2, adj f26,f115,f121,f143
  f115: bspline ~4.98x1.79mm, area 0.8mm2, adj f26,f104,f114,f144
  f116: bspline ~2.25x1.56mm, area 0.4mm2, adj f25,f95,f104,f145
  f117: cylinder r=0.38mm len=28.6mm, axis (1,0,0), area 34.2mm2, adj f25,f26,f118,f163
  f118: torus R=17.78mm, axis (0,0,-1), area 66.9mm2, adj f25,f26,f117,f119
  f119: cylinder r=0.38mm len=4.56mm, axis (-1,0,0), area 5.5mm2, adj f25,f26,f118,f120
  f120: torus R=4.45mm, axis (0,0,-1), area 15.6mm2, adj f25,f26,f119,f121,f122,f147
  f121: bspline ~0.57x0.43mm, area 0.1mm2, adj f26,f114,f120,f147
  f122: bspline ~0.6x0.46mm, area 0.1mm2, adj f25,f95,f120,f147
  f123: plane 3.05x1.52mm, normal (0,1,0), area 3.6mm2, adj f31,f124
  f124: torus R=1.52mm, axis (0,-1,0), area 31.8mm2, adj f31,f32,f123,f148
  f125: bspline ~3.72x2.94mm, area 7.4mm2, adj f32,f33,f148,f149
  f126: bspline ~7.38x2.8mm, area 16.4mm2, adj f30,f32,f63,f149
  f127: bspline ~7.38x2.8mm, area 16.4mm2, adj f29,f30,f32,f93
  f128: cylinder r=8mm len=16mm, axis (0,-1,0), area 334.9mm2, adj f0,f29,f31,f129
  f129: cone r=8.13mm half-angle=21.8deg, axis (0,-1,0), area 200.9mm2, adj f29,f31,f32,f128
  f130: plane 43.04x31.62mm, normal (0,0,-1), area 503.8mm2, adj f131,f134
  f131: bspline ~44.22x36.99mm, area 204.3mm2, adj f35,f54,f130,f132,f133,f135
  f132: bspline ~15.12x5.32mm, area 44.6mm2, adj f44,f55,f131,f134
  f133: bspline ~10.58x3.79mm, area 20.6mm2, adj f44,f56,f131,f134
  f134: bspline ~11.85x7.26mm, area 42.8mm2, adj f44,f130,f132,f133
  f135: bspline ~1.33x0.73mm, area 0.6mm2, adj f60,f61,f62,f131
  f136: plane 43.04x31.62mm, normal (0,0,-1), area 503.8mm2, adj f137,f140
  f137: bspline ~44.22x36.99mm, area 204.3mm2, adj f65,f84,f136,f138,f139,f141
  f138: bspline ~15.12x5.32mm, area 44.6mm2, adj f74,f85,f137,f140
  f139: bspline ~10.58x3.79mm, area 20.6mm2, adj f74,f86,f137,f140
  f140: bspline ~11.85x7.26mm, area 42.8mm2, adj f74,f136,f138,f139
  f141: bspline ~1.33x0.73mm, area 0.6mm2, adj f90,f91,f92,f137
  f142: plane 43.04x31.62mm, normal (0,0,-1), area 503.8mm2, adj f143,f146
  f143: bspline ~44.22x36.99mm, area 204.3mm2, adj f95,f114,f142,f144,f145,f147
  f144: bspline ~15.12x5.32mm, area 44.6mm2, adj f104,f115,f143,f146
  f145: bspline ~10.58x3.79mm, area 20.6mm2, adj f104,f116,f143,f146
  f146: bspline ~11.85x7.26mm, area 42.8mm2, adj f104,f142,f144,f145
  f147: bspline ~1.33x0.73mm, area 0.6mm2, adj f120,f121,f122,f143
  f148: bspline ~3.14x2.99mm, area 2.6mm2, adj f33,f124,f125
  f149: plane 59.75x16.13mm, normal (0,0,-1), area 919.8mm2, adj f32,f33,f34,f36,f45,f46,f63,f64
  f150: plane 153.31x12.7mm, normal (0,-1,0), area 1947.1mm2, adj f151,f152,f154,f155
  f151: plane 220.09x153.31mm, normal (0,0,-1), area 942mm2, adj f0,f150,f153,f154,f155,f161,f162,f163
  f152: plane 220.09x153.31mm, normal (0,0,1), area 33742.1mm2, adj f150,f153,f154,f155
  f153: plane 153.31x12.7mm, normal (0,1,0), area 1947.1mm2, adj f151,f152,f154,f155
  f154: plane 220.09x12.7mm, normal (1,0,0), area 2795.1mm2, adj f150,f151,f152,f153
  f155: plane 220.09x12.7mm, normal (-1,0,0), area 2795.1mm2, adj f150,f151,f152,f153
  f156: sphere r=3.17mm, area 63.3mm2, adj f25
  f157: sphere r=3.17mm, area 63.3mm2, adj f31
  f158: sphere r=3.17mm, area 63.3mm2, adj f27
  f159: sphere r=3.17mm, area 63.3mm2, adj f26
  f160: sphere r=3.17mm, area 63.3mm2, adj f28
  f161: plane 217.55x9.65mm, normal (-1,0,-0.1), area 2100.9mm2, adj f0,f31,f151,f162
  f162: plane 150.9x9.78mm, normal (0,-1,-0.1), area 1448.7mm2, adj f3,f7,f11,f15,f19,f23,f27,f31
  f163: plane 217.62x9.73mm, normal (1,0,-0.1), area 2100.2mm2, adj f0,f25,f26,f27,f28,f57,f87,f117
  f164: cylinder r=0.64mm len=52.32mm, axis (0,-1,0), area 104.3mm2, adj f23,f27,f42,f162
  f165: cylinder r=0.64mm len=55.03mm, axis (0,-1,0), area 109.6mm2, adj f24,f28,f42,f72
  f166: cylinder r=0.64mm len=27.82mm, axis (0,-1,0), area 55.4mm2, adj f0,f21,f25,f102
  f167: cylinder r=0.64mm len=55.03mm, axis (0,-1,0), area 109.6mm2, adj f22,f26,f72,f102
  f168: cylinder r=0.64mm len=52.21mm, axis (0,-1,0), area 104.1mm2, adj f19,f23,f41,f162
  f169: cylinder r=0.64mm len=54.8mm, axis (0,-1,0), area 109.2mm2, adj f20,f24,f41,f71
  f170: cylinder r=0.64mm len=27.7mm, axis (0,-1,0), area 55.2mm2, adj f0,f17,f21,f101
  f171: cylinder r=0.64mm len=54.8mm, axis (0,-1,0), area 109.2mm2, adj f18,f22,f71,f101
  f172: cylinder r=0.64mm len=52.06mm, axis (0,-1,0), area 103.8mm2, adj f15,f19,f40,f162
  f173: cylinder r=0.64mm len=54.5mm, axis (0,-1,0), area 108.6mm2, adj f16,f20,f40,f70
  f174: cylinder r=0.64mm len=27.55mm, axis (0,-1,0), area 54.9mm2, adj f0,f13,f17,f100
  f175: cylinder r=0.64mm len=54.5mm, axis (0,-1,0), area 108.6mm2, adj f14,f18,f70,f100
  f176: cylinder r=0.64mm len=51.9mm, axis (0,-1,0), area 103.3mm2, adj f11,f15,f39,f49,f162
  f177: cylinder r=0.64mm len=54.18mm, axis (0,-1,0), area 107.6mm2, adj f12,f16,f39,f49,f69,f79
  f178: cylinder r=0.64mm len=27.4mm, axis (0,-1,0), area 54.4mm2, adj f0,f9,f13,f99,f109
  f179: cylinder r=0.64mm len=54.18mm, axis (0,-1,0), area 107.6mm2, adj f10,f14,f69,f79,f99,f109
  f180: cylinder r=0.64mm len=52.22mm, axis (0,-1,0), area 104.1mm2, adj f7,f11,f48,f162
  f181: cylinder r=0.64mm len=54.82mm, axis (0,-1,0), area 109.1mm2, adj f8,f12,f48,f78
  f182: cylinder r=0.64mm len=27.72mm, axis (0,-1,0), area 55.2mm2, adj f0,f5,f9,f108
  f183: cylinder r=0.64mm len=54.82mm, axis (0,-1,0), area 109.1mm2, adj f6,f10,f78,f108
  f184: cylinder r=0.64mm len=52.57mm, axis (0,-1,0), area 104.7mm2, adj f3,f7,f47,f162
  f185: cylinder r=0.64mm len=55.51mm, axis (0,-1,0), area 110.4mm2, adj f4,f8,f47,f77
  f186: cylinder r=0.64mm len=28.06mm, axis (0,-1,0), area 55.8mm2, adj f0,f1,f5,f107
  f187: cylinder r=0.64mm len=55.51mm, axis (0,-1,0), area 110.4mm2, adj f2,f6,f77,f107
  f188: cylinder r=0.64mm len=52.68mm, axis (0,-1,0), area 104.8mm2, adj f3,f31,f46,f162
  f189: cylinder r=0.64mm len=55.74mm, axis (0,-1,0), area 110.7mm2, adj f4,f46,f76,f149
  f190: cylinder r=0.64mm len=28.18mm, axis (0,-1,0), area 56mm2, adj f0,f1,f29,f106
  f191: cylinder r=0.64mm len=55.74mm, axis (0,-1,0), area 110.7mm2, adj f2,f30,f76,f106
PLACE A at identity
PLACE B at identity
MATE fastened A.f164 <-> B.f26  axis (0,0,1) through (0,-92.71,0)mm
